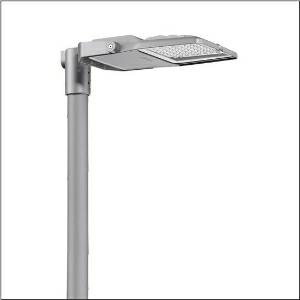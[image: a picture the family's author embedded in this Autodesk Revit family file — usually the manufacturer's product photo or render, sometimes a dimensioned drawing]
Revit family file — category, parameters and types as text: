
# Revit family: floodlight_fl_21_iq_mini___pl52_5xa7772c4d3a_40ba
name_source: partatom
category: Lighting Fixtures
units: mm (PartAtom-declared; Revit-internal decimal feet)

## family parameters
Cut with Voids When Loaded = No
Host = Face
Light Source = No
Part Type = Normal
Room Calculation Point = No
Round Connector Dimension = Use Diameter
Shared = No

## types (1)
- --- (1 x LED, 12720 lm, 87.2 W, 4000K)
    Apparent Load = 87 VA
    CIE Flux Codes = 26 60 98 100 100
    Color Rendering = 70
    Color Temperature = 4000K
    Default Elevation = 1800 mm
    Description = Floodlight FL 21 iQ mini, floodlight, primary light control with lens, of PMMA, primary optical cover: protective disc, of toughened safety glass, transparent, light distribution: PL52, light emission: direct distribution, installation type: surface-mounted, lamps: LED, High Power LED, rated values: 12.720lm | 87,2W | 145,9lm/W (begin service life); end service life: 12.720lm | 92,1W; at 50% lumin. flux: 6.360lm | 40,2W | 158,2lm/W, colour temperature: 4000K, colour rendering: CRI > 70, light colour: 740, light setting 1 begin service life: 100% | 12.720lm | 87,2W | 145,9lm/W | 4.000K, light setting 1 end service life: 92,1W, further light settings possible, control: pre-setting: linear dimming characteristic, Auto-Match, Temp-Guard, Night-Set, Smart-Wire, Desk-Remote (wireless, voltage-free reading and setting of iQ features in the workshop via application-optimized NFC function/RFID function), optimised constant luminous flux control (CLO 2.0), Light-Fading, Lumen-Switch, with terminal, 6-pole, mains connection: 220..240V, AC, 50/60Hz, luminaire housing, of diecast aluminium, powder-coated, SITECO metallic grey (DB 702S), corrosivity category C5 mid according to DIN EN ISO 12944suitable for swimming poolschlorine-resistant, sealing non-destructively replaceable, please order mast flange separately, mast bracket, of steel, galvanised, powder-coated, protection rating (complete): IP66, insulation class (complete): insulation class II (safety insulation), certification: CE, ENEC, VDE, protection symbol: D, impact resistance: IK08, permissible operating ambient temperature: -40..+40°C, permissible operating ambient temperature for outdoor applications: -40..+50°C, standard: DIN EN 12944, LABS conformity tested according to VDMA 24364:2018-05, packaging unit: 1 piece

Light Distribution: PL52
    Height = 70 mm
    Lamp = 1 x LED
    Lamp Light Flux = 12720 lm
    Lamp Power = 87.2 W
    Lamp count = 1
    Length = 485 mm
    Luminous efficacy = 146 lm/W
    Manufacturer = Siteco
    ModVariant = No
    Model = 5XA7772C4D3A
    Number of Poles = 1
    OnlyDefault = Yes
    Power Factor = 1
    Product Name = Floodlight FL 21 iQ mini | PL52
    Product group = floodlight | pylon annexe
    ProductGroupID = 6201
    Protection Class = Protection class II
    Protection Degree = IP 66
    RLX_Detail_Level = 1
    RLX_Emergency_Light_Flux = 0 lm
    RLX_Emergency_Type = 0
    RLX_Emergency_Type_DB = No
    RlxData = <blob elided: 101745 chars, md5=e0dae3a7>
    Socket = socket
    Standby Power = 0 W
    System Light Flux = 12720 lm
    System Power = 87 W
    Type Comments = factory setting: luminous flux: 100 % | dim-lin: 254 | 456 mA
    Type Image = l_1007125.jpg
    URL = http://relux.com
    VarID = @adj_163629
    Voltage = 0 V
    Weight = 0.00 kg
    Width = 337 mm

## geometry (parser evidence)
native form markers: Blend x4, Sweep x13
no freeform markers — native parametric forms only
